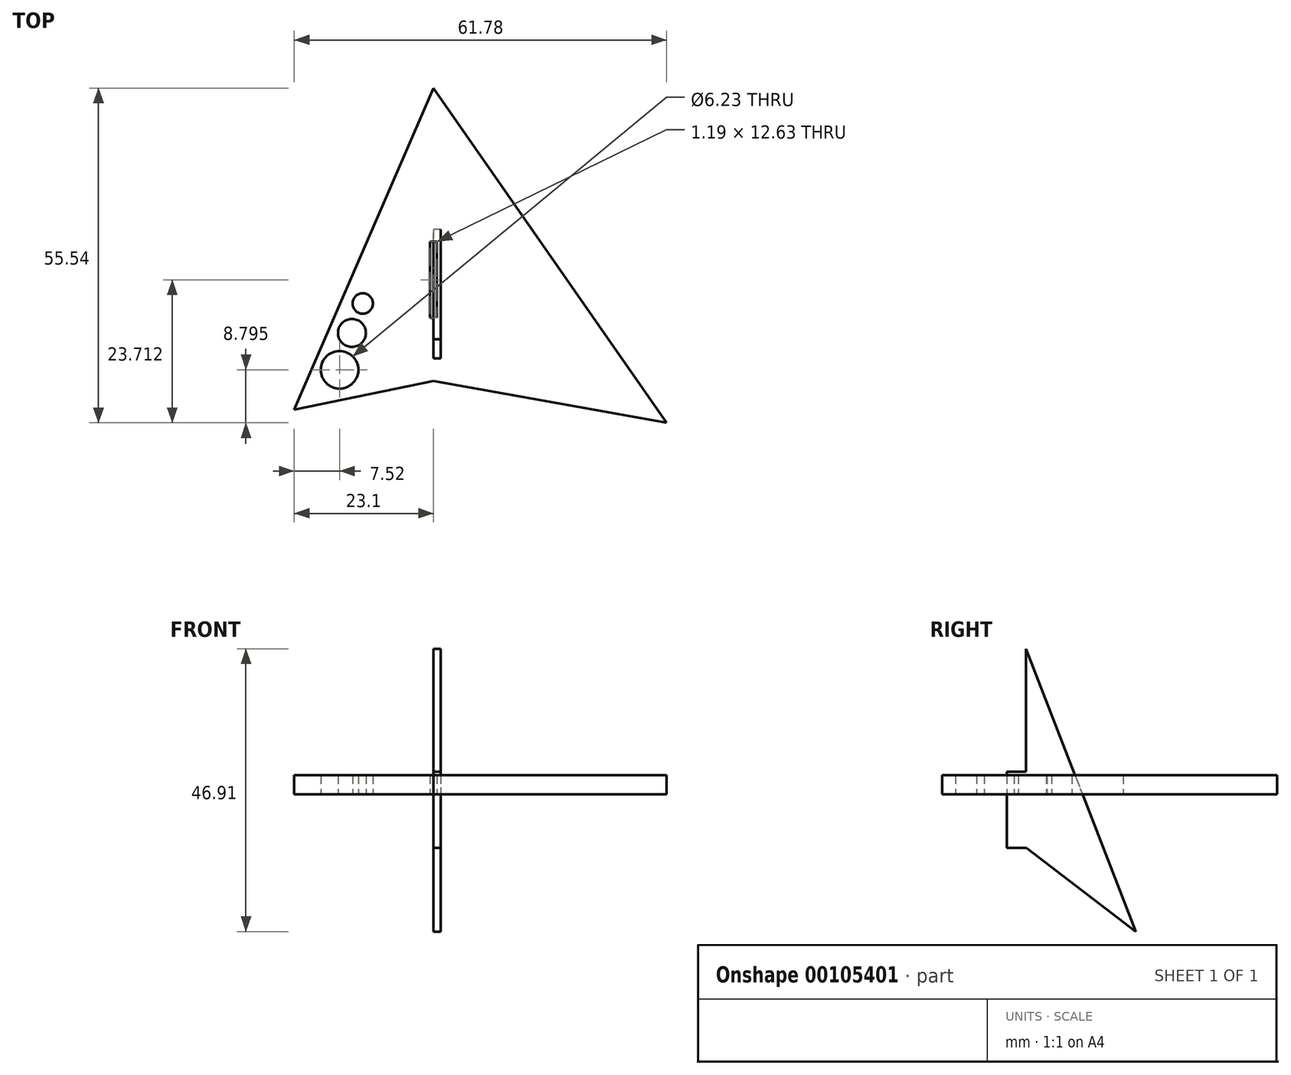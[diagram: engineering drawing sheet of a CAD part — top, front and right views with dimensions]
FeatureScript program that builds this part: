
annotation { "Feature Type Name" : "Feature", "Feature Type Description" : "" }
export const myFeature = defineFeature(function(context is Context, id is Id, definition is map)
    precondition{}
    {
        {
            var Q0;
            Q0=qCreatedBy(makeId("Top.planeOp"),FACE);
            var sketch = newSketch(context, id + "F0", { "sketchPlane" : qUnion([Q0])});
            skLineSegment(sketch, "E0", {"start": v(0, 44.82) * mm, "end": v(-23.1, -8.52) * mm});
            skLineSegment(sketch, "E1", {"start": v(-23.1, -8.52) * mm, "end": v(0, -3.76) * mm});
            skLineSegment(sketch, "E2", {"start": v(0, -3.76) * mm, "end": v(38.68, -10.72) * mm});
            skLineSegment(sketch, "E3", {"start": v(38.68, -10.72) * mm, "end": v(0, 44.82) * mm});
            skCircle(sketch, "E4", {"center": v(-11.73, 9.08) * mm, "radius": 1.69 * mm});
            skCircle(sketch, "E5", {"center": v(-13.52, 4.19) * mm, "radius": 2.32 * mm});
            skCircle(sketch, "E6", {"center": v(-15.58, -1.92) * mm, "radius": 3.12 * mm});
            skLineSegment(sketch, "E7.bottom", {"start": v(0.6, 19.3) * mm, "end": v(-0.6, 19.3) * mm});
            skLineSegment(sketch, "E7.top", {"start": v(0.6, 6.68) * mm, "end": v(-0.6, 6.68) * mm});
            skLineSegment(sketch, "E7.left", {"start": v(0.6, 19.3) * mm, "end": v(0.6, 6.68) * mm});
            skLineSegment(sketch, "E7.right", {"start": v(-0.6, 19.3) * mm, "end": v(-0.6, 6.68) * mm});
            skPoint(sketch, "E7.middle", {"position": v(0, 13) * mm});
            skLineSegment(sketch, "E8", {"start": v(-13.83, 12.88) * mm, "end": v(-20.98, -3.63) * mm});
            skSolve(sketch);
        }
        {
            var Q0;
            Q0=makeQuery(id+"F0.imprint","IMPRINT",FACE,{"disambiguationData":[TD([[makeQuery(id+"F0.imprint","IMPRINT",EDGE,{"derivedFrom":sQuery(id+"F0.wireOp",EDGE,"E0")}),1.0]])]});
            extrude(context, id + "F1", {"entities" : qUnion([Q0]), "depth" : 3.17 * mm});
        }
        {
            var Q0;
            Q0=qCreatedBy(makeId("Right.planeOp"),FACE);
            var sketch = newSketch(context, id + "F2", { "sketchPlane" : qUnion([Q0])});
            skLineSegment(sketch, "E9.bottom", {"start": v(0, 3.71) * mm, "end": v(3.17, 3.71) * mm});
            skLineSegment(sketch, "E9.top", {"start": v(0, -8.91) * mm, "end": v(3.21, -8.91) * mm});
            skLineSegment(sketch, "E9.left", {"start": v(0, 3.71) * mm, "end": v(0, -8.91) * mm});
            skLineSegment(sketch, "E10", {"start": v(3.17, 3.71) * mm, "end": v(3.17, 24.13) * mm});
            skLineSegment(sketch, "E11", {"start": v(3.17, 24.13) * mm, "end": v(21.38, -22.78) * mm});
            skLineSegment(sketch, "E12", {"start": v(21.38, -22.78) * mm, "end": v(3.21, -8.91) * mm});
            skSolve(sketch);
        }
        {
            var Q0;
            Q0 = qSketchRegion(id + "F2", true);
            extrude(context, id + "F3", {"entities" : qUnion([Q0]), "depth" : 1.2 * mm});
        }
    });
